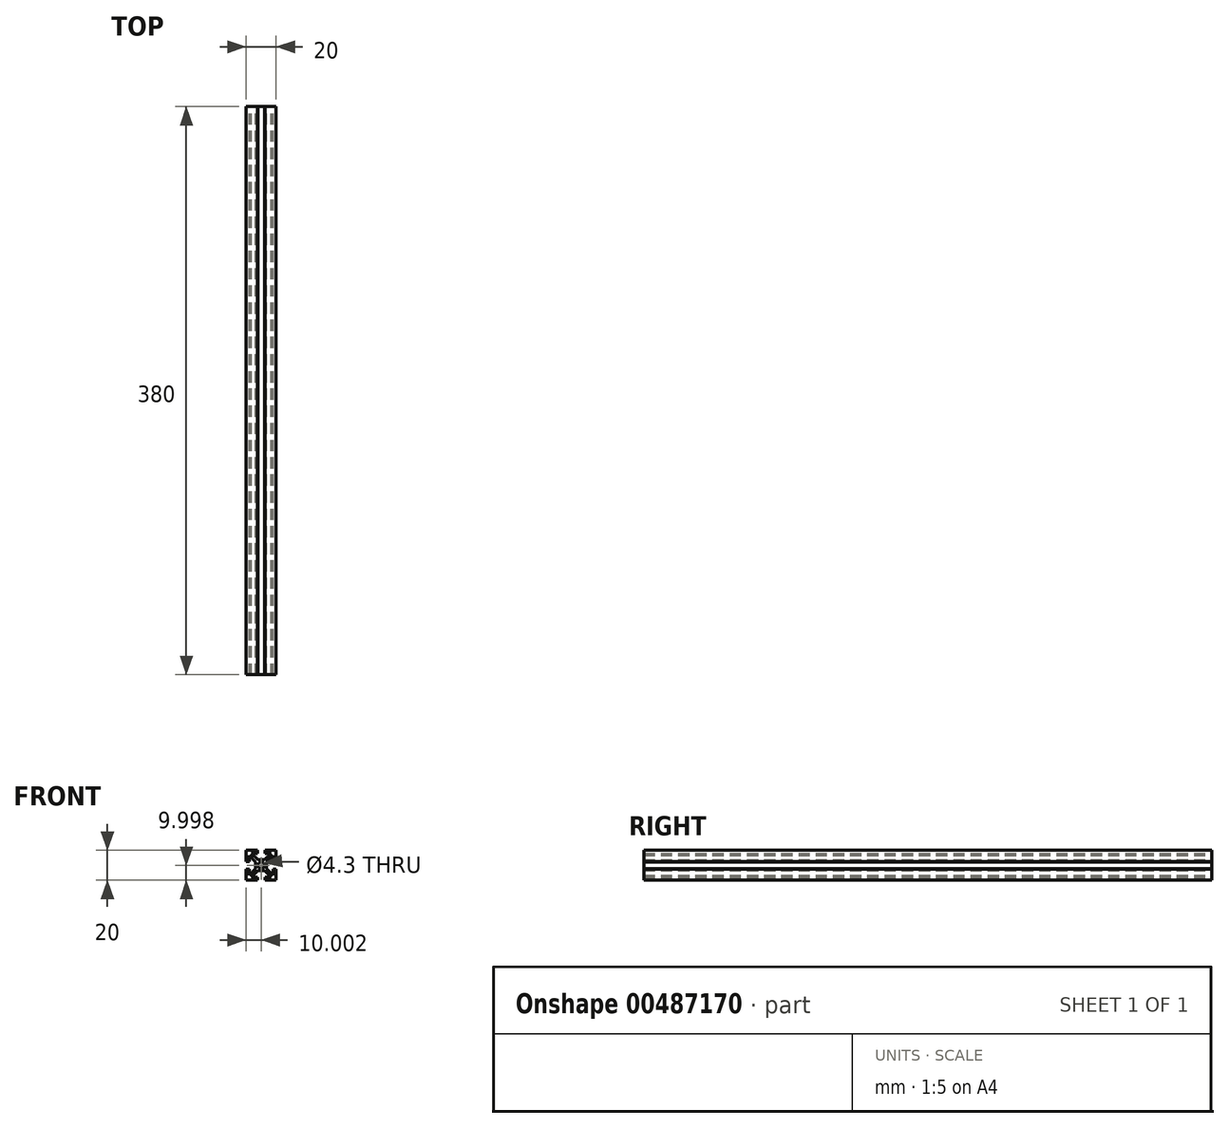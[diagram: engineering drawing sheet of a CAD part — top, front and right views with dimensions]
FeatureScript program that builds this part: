
annotation { "Feature Type Name" : "Feature", "Feature Type Description" : "" }
export const myFeature = defineFeature(function(context is Context, id is Id, definition is map)
    precondition{}
    {
        {
            var Q0;
            Q0=qCreatedBy(makeId("Front.planeOp"),FACE);
            var sketch = newSketch(context, id + "F0", { "sketchPlane" : qUnion([Q0])});
            skLineSegment(sketch, "E0.bottom", {"start": v(-9.74, 9.77) * mm, "end": v(-2.24, 9.77) * mm});
            skLineSegment(sketch, "E0.left", {"start": v(-9.74, 9.77) * mm, "end": v(-9.74, 2.27) * mm});
            skLineSegment(sketch, "E0.right", {"start": v(10.26, 9.77) * mm, "end": v(10.26, 2.27) * mm});
            skArc(sketch, "E1", {"start": v(2.41, -0.23) * mm, "mid": v(0.26, 1.92) * mm, "end": v(-1.89, -0.23) * mm});
            skLineSegment(sketch, "E2.bottom", {"start": v(-1.97, 3.42) * mm, "end": v(2.5, 3.42) * mm});
            skLineSegment(sketch, "E2.left", {"start": v(-3.39, 2) * mm, "end": v(-3.39, -0.23) * mm});
            skLineSegment(sketch, "E2.right", {"start": v(3.91, 2) * mm, "end": v(3.91, -0.23) * mm});
            skLineSegment(sketch, "E3", {"start": v(-2.24, 9.77) * mm, "end": v(-2.24, 7.77) * mm});
            skLineSegment(sketch, "E4", {"start": v(-2.24, 7.77) * mm, "end": v(-6.32, 7.77) * mm});
            skLineSegment(sketch, "E5", {"start": v(2.76, 9.77) * mm, "end": v(2.76, 7.77) * mm});
            skPoint(sketch, "E5.endSnap0", {"position": v(-5.99, 7.77) * mm});
            skLineSegment(sketch, "E6", {"start": v(2.76, 7.77) * mm, "end": v(6.85, 7.77) * mm});
            skLineSegment(sketch, "E7", {"start": v(-7.74, 6.35) * mm, "end": v(-7.74, 2.27) * mm});
            skLineSegment(sketch, "E8", {"start": v(-7.74, 2.27) * mm, "end": v(-9.74, 2.27) * mm});
            skLineSegment(sketch, "E9", {"start": v(-7.74, 6.35) * mm, "end": v(-3.39, 2) * mm});
            skLineSegment(sketch, "E10", {"start": v(-1.97, 3.42) * mm, "end": v(-6.32, 7.77) * mm});
            skPoint(sketch, "E10.endSnap0", {"position": v(-6.32, -0.18) * mm});
            skLineSegment(sketch, "E11", {"start": v(8.26, 6.35) * mm, "end": v(8.26, 2.27) * mm});
            skLineSegment(sketch, "E12", {"start": v(8.26, 2.27) * mm, "end": v(10.26, 2.27) * mm});
            skPoint(sketch, "E13.orphan", {"position": v(10.26, 7.77) * mm});
            skLineSegment(sketch, "E14", {"start": v(2.5, 3.42) * mm, "end": v(6.85, 7.77) * mm});
            skLineSegment(sketch, "E15", {"start": v(3.91, 2) * mm, "end": v(8.26, 6.35) * mm});
            skPoint(sketch, "E16.orphan", {"position": v(-9.74, 7.77) * mm});
            skPoint(sketch, "E17.orphan", {"position": v(-3.39, 3.42) * mm});
            skPoint(sketch, "E18.orphan", {"position": v(3.91, 3.42) * mm});
            skLineSegment(sketch, "E19", {"start": v(-9.74, -0.23) * mm, "end": v(10.26, -0.23) * mm, "construction": true});
            skPoint(sketch, "E0.top.end.orphan", {"position": v(10.26, -10.23) * mm});
            skPoint(sketch, "E0.top.start.orphan", {"position": v(-9.74, -10.23) * mm});
            skLineSegment(sketch, "E20.MirrorCS", {"start": v(-9.74, -10.23) * mm, "end": v(-9.74, -2.73) * mm});
            skLineSegment(sketch, "E21.MirrorCS", {"start": v(-7.74, -2.73) * mm, "end": v(-9.74, -2.73) * mm});
            skLineSegment(sketch, "E22.MirrorCS", {"start": v(-7.74, -6.82) * mm, "end": v(-7.74, -2.73) * mm});
            skLineSegment(sketch, "E23.MirrorCS", {"start": v(-7.74, -6.82) * mm, "end": v(-3.39, -2.47) * mm});
            skLineSegment(sketch, "E24.MirrorCS", {"start": v(-3.39, -2.47) * mm, "end": v(-3.39, -0.23) * mm});
            skArc(sketch, "E25.MirrorCS", {"start": v(2.41, -0.23) * mm, "mid": v(0.26, -2.38) * mm, "end": v(-1.89, -0.23) * mm});
            skLineSegment(sketch, "E26.MirrorCS", {"start": v(-1.97, -3.88) * mm, "end": v(-6.32, -8.23) * mm});
            skLineSegment(sketch, "E27.MirrorCS", {"start": v(-1.97, -3.88) * mm, "end": v(2.5, -3.88) * mm});
            skLineSegment(sketch, "E28.MirrorCS", {"start": v(-2.24, -8.23) * mm, "end": v(-6.32, -8.23) * mm});
            skLineSegment(sketch, "E29.MirrorCS", {"start": v(-2.24, -10.23) * mm, "end": v(-2.24, -8.23) * mm});
            skLineSegment(sketch, "E30.MirrorCS", {"start": v(-9.74, -10.23) * mm, "end": v(-2.24, -10.23) * mm});
            skLineSegment(sketch, "E31.MirrorCS", {"start": v(2.76, -10.23) * mm, "end": v(2.76, -8.23) * mm});
            skLineSegment(sketch, "E32.MirrorCS", {"start": v(2.76, -8.23) * mm, "end": v(6.85, -8.23) * mm});
            skLineSegment(sketch, "E33.MirrorCS", {"start": v(2.5, -3.88) * mm, "end": v(6.85, -8.23) * mm});
            skLineSegment(sketch, "E34.MirrorCS", {"start": v(3.91, -2.47) * mm, "end": v(8.26, -6.82) * mm});
            skLineSegment(sketch, "E35.MirrorCS", {"start": v(8.26, -6.82) * mm, "end": v(8.26, -2.73) * mm});
            skLineSegment(sketch, "E36.MirrorCS", {"start": v(8.26, -2.73) * mm, "end": v(10.26, -2.73) * mm});
            skLineSegment(sketch, "E37.MirrorCS", {"start": v(10.26, -10.23) * mm, "end": v(10.26, -2.73) * mm});
            skLineSegment(sketch, "E38.MirrorCS", {"start": v(3.91, -2.47) * mm, "end": v(3.91, -0.23) * mm});
            skLineSegment(sketch, "E39.trimOffspring", {"start": v(2.76, 9.77) * mm, "end": v(10.26, 9.77) * mm});
            skLineSegment(sketch, "E40.trimOffspring", {"start": v(2.76, -10.23) * mm, "end": v(10.26, -10.23) * mm});
            skSolve(sketch);
        }
        {
            var Q0;
            Q0 = qSketchRegion(id + "F0", true);
            extrude(context, id + "F1", {"entities" : qUnion([Q0]), "depth" : 190 * mm, "hasSecondDirection" : true, "secondDirectionOppositeDirection" : true, "secondDirectionDepth" : 190 * mm});
        }
    });
